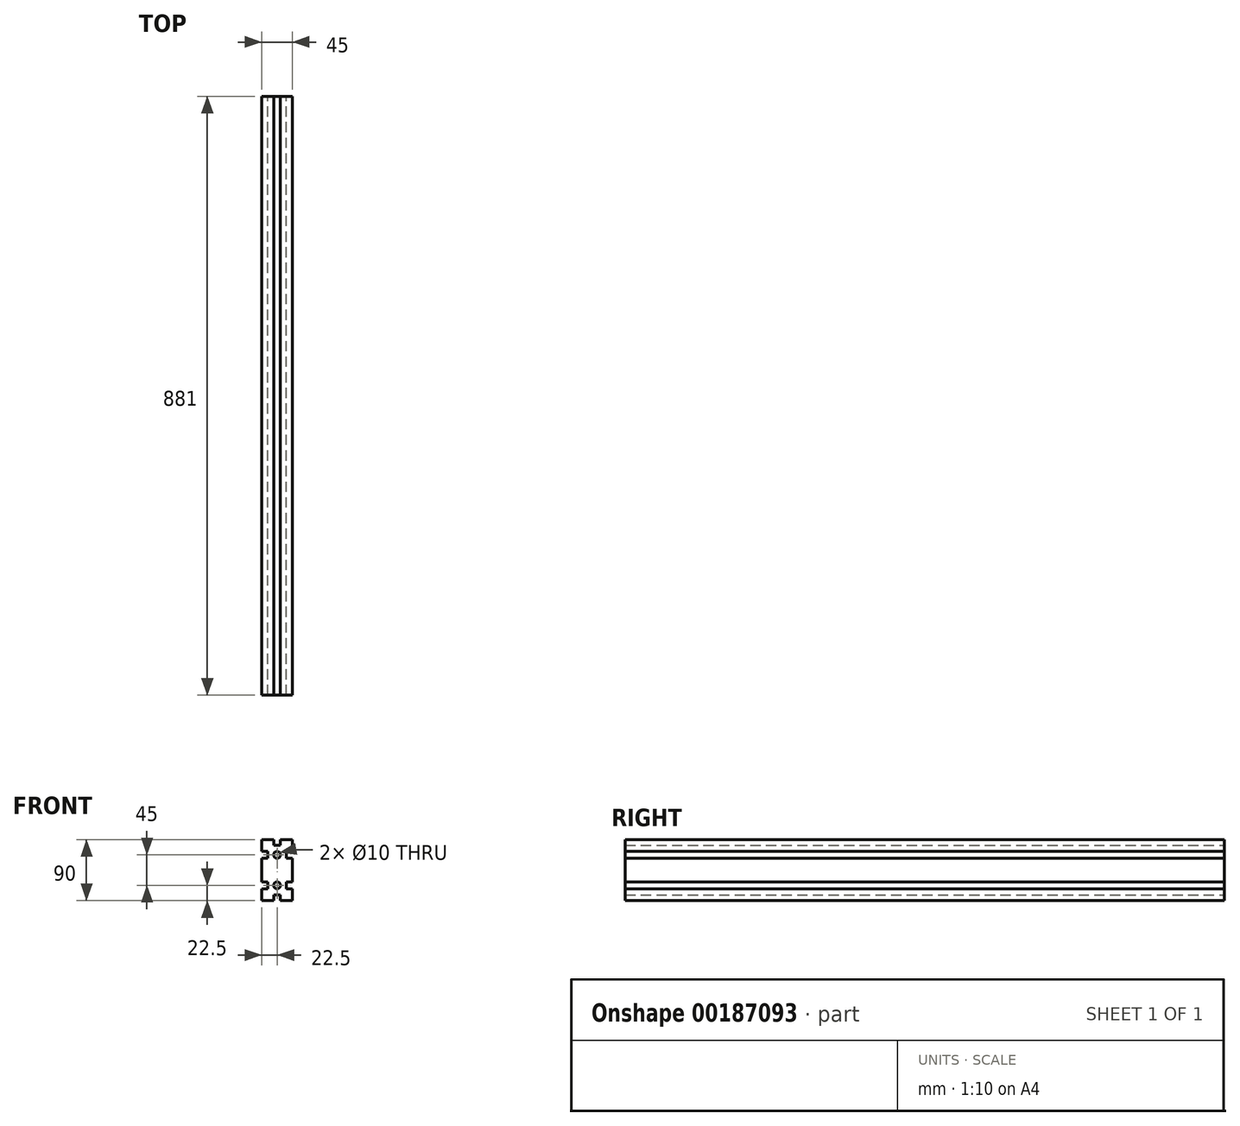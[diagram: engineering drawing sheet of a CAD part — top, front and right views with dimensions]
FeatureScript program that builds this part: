
annotation { "Feature Type Name" : "Feature", "Feature Type Description" : "" }
export const myFeature = defineFeature(function(context is Context, id is Id, definition is map)
    precondition{}
    {
        {
            var Q0;
            Q0=qCreatedBy(makeId("Front.planeOp"),FACE);
            var sketch = newSketch(context, id + "F0", { "sketchPlane" : qUnion([Q0])});
            skLineSegment(sketch, "E0.bottom", {"start": v(22.5, -45) * mm, "end": v(5, -45) * mm});
            skLineSegment(sketch, "E0.top", {"start": v(22.5, 45) * mm, "end": v(5, 45) * mm});
            skLineSegment(sketch, "E0.left", {"start": v(22.5, -45) * mm, "end": v(22.5, -27.5) * mm});
            skLineSegment(sketch, "E0.right", {"start": v(-22.5, -45) * mm, "end": v(-22.5, -27.5) * mm});
            skPoint(sketch, "E0.middle", {"position": v(0, 0) * mm});
            skCircle(sketch, "E1", {"center": v(0, 22.5) * mm, "radius": 5 * mm});
            skCircle(sketch, "E2", {"center": v(0, -22.5) * mm, "radius": 5 * mm});
            skLineSegment(sketch, "E3", {"start": v(-5, 45) * mm, "end": v(-5, 36.25) * mm});
            skLineSegment(sketch, "E4", {"start": v(5, 45) * mm, "end": v(5, 36.25) * mm});
            skLineSegment(sketch, "E5", {"start": v(-22.5, 27.5) * mm, "end": v(-13.75, 27.5) * mm});
            skLineSegment(sketch, "E6", {"start": v(-22.5, 17.5) * mm, "end": v(-13.75, 17.5) * mm});
            skLineSegment(sketch, "E7", {"start": v(-22.5, -17.5) * mm, "end": v(-13.75, -17.5) * mm});
            skLineSegment(sketch, "E8", {"start": v(-22.5, -27.5) * mm, "end": v(-13.75, -27.5) * mm});
            skLineSegment(sketch, "E9", {"start": v(-13.75, 27.5) * mm, "end": v(-13.75, 17.5) * mm});
            skLineSegment(sketch, "E10", {"start": v(13.75, 27.5) * mm, "end": v(13.75, 17.5) * mm});
            skLineSegment(sketch, "E11", {"start": v(-5, 36.25) * mm, "end": v(5, 36.25) * mm});
            skPoint(sketch, "E12.orphan", {"position": v(-22.5, 36.25) * mm});
            skLineSegment(sketch, "E13.trimOffspring", {"start": v(13.75, 17.5) * mm, "end": v(22.5, 17.5) * mm});
            skLineSegment(sketch, "E14.trimOffspring", {"start": v(-22.5, 27.5) * mm, "end": v(-22.5, 45) * mm});
            skLineSegment(sketch, "E15.trimOffspring", {"start": v(-13.75, -17.5) * mm, "end": v(-13.75, -27.5) * mm});
            skLineSegment(sketch, "E16.trimOffspring", {"start": v(13.75, 27.5) * mm, "end": v(22.5, 27.5) * mm});
            skLineSegment(sketch, "E17.trimOffspring", {"start": v(22.5, 27.5) * mm, "end": v(22.5, 45) * mm});
            skLineSegment(sketch, "E18.trimOffspring", {"start": v(-5, 45) * mm, "end": v(-22.5, 45) * mm});
            skLineSegment(sketch, "E19.trimOffspring", {"start": v(13.75, -17.5) * mm, "end": v(13.75, -27.5) * mm});
            skLineSegment(sketch, "E20.trimOffspring", {"start": v(13.75, -17.5) * mm, "end": v(22.5, -17.5) * mm});
            skLineSegment(sketch, "E21.trimOffspring", {"start": v(-5, -36.25) * mm, "end": v(-5, -45) * mm});
            skLineSegment(sketch, "E22.trimOffspring", {"start": v(13.75, -27.5) * mm, "end": v(22.5, -27.5) * mm});
            skLineSegment(sketch, "E23.trimOffspring", {"start": v(5, -36.25) * mm, "end": v(5, -45) * mm});
            skLineSegment(sketch, "E24.trimOffspring", {"start": v(22.5, -17.5) * mm, "end": v(22.5, 17.5) * mm});
            skLineSegment(sketch, "E25.trimOffspring", {"start": v(-22.5, -17.5) * mm, "end": v(-22.5, 17.5) * mm});
            skLineSegment(sketch, "E26.trimOffspring", {"start": v(-5, -45) * mm, "end": v(-22.5, -45) * mm});
            skPoint(sketch, "E27.orphan", {"position": v(13.75, -45) * mm});
            skLineSegment(sketch, "E28.trimOffspring", {"start": v(-5, -36.25) * mm, "end": v(5, -36.25) * mm});
            skPoint(sketch, "E29.start.orphan", {"position": v(-22.5, -36.25) * mm});
            skPoint(sketch, "E30.trimOffspring.end.orphan", {"position": v(-13.75, -45) * mm});
            skSolve(sketch);
        }
        {
            var Q0;
            Q0=makeQuery(id+"F0.imprint","IMPRINT",FACE,{"disambiguationData":[TD([[makeQuery(id+"F0.imprint","IMPRINT",EDGE,{"derivedFrom":sQuery(id+"F0.wireOp",EDGE,"E0.bottom")}),-1.0]])]});
            extrude(context, id + "F1", {"entities" : qUnion([Q0]), "depth" : 881 * mm});
        }
    });
